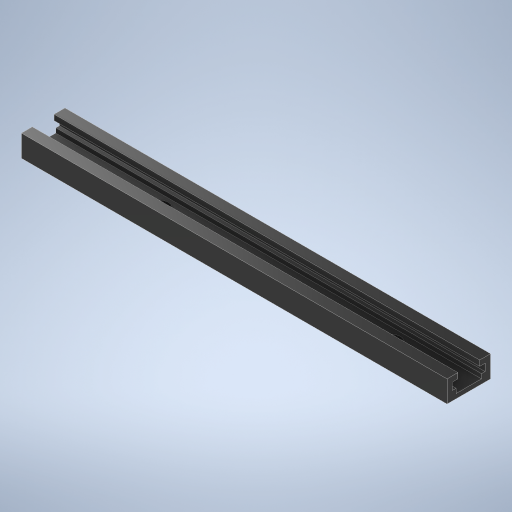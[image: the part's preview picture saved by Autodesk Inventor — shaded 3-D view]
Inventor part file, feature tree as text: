
AUTODESK INVENTOR PART (.ipt)
format: ipt  version: 2024 (Build 280153000, 153)  size: 290,304 bytes
history: native  units: in
note: dims shown in document units (in); Inventor stores cm internally (conversion verified against a paired STEP export)
features: extrude x2, sketch x2, projected_geometry x1
ambient origin geometry x8: Origin, YZ Plane, XZ Plane, XY Plane, X Axis, Y Axis, Z Axis, Center Point
bodies: Solid1 (feature_tree)
feature tree (5):
  extrude  "Extrusion1"  Depth=0.375in
  extrude  "Extrusion2"  Depth=0.2812in
  sketch  "Sketch1"  dims[d3=7.334in d4=0.0in d20=0.375in]
  sketch  "Sketch2"  dims[d21=0.75in d22=0.2812in d23=0.1562in d24=0.2812in d25=0.1875in d26=0.2188in d27=2.0in d28=4.0in d29=4.0in d30=8.0in d31=0.3125in d32=0.3125in d33=0.3125in d34=0.0in d35=0.0in d36=0.5in d37=0.0344in d38=0.5in d39=0.0344in]
  projected_geometry  "Projected Loop1"
